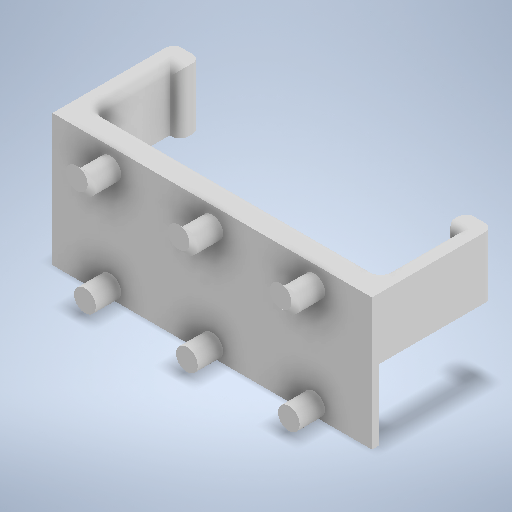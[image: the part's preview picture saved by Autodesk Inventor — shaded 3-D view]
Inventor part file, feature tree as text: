
AUTODESK INVENTOR PART (.ipt)
format: ipt  version: 2025.2 (Build 292293000, 293)  size: 474,112 bytes
history: native  units: mm
features: other x10, sketch x6, extrude x5, pattern_linear x3, fillet x3, direct_edit x3, move_body x3, chamfer x2, loft x1
ambient origin geometry x8: Origin, YZ Plane, XZ Plane, XY Plane, X Axis, Y Axis, Z Axis, Center Point
bodies: Body1 (feature_tree)
feature tree (36):
  other  "Твердое тело1"
  extrude  "Выдавливание1"  Depth=1.85mm TaperAngle=0.0deg
  extrude  "Выдавливание2"  Depth=55.2mm
  pattern_linear  "Прямоуг.массив1"  Spacing1=32.25mm  [1 undecoded]
  extrude  "Выдавливание3"  Depth=5.3mm
  extrude  "Выдавливание4"  Depth=6.2mm TaperAngle=0.0deg
  fillet  "Сопряжение1"  Radius=20.0mm
  pattern_linear  "Прямоуг.массив2"  Spacing1=24.95mm  [1 undecoded]
  fillet  "Сопряжение2"  Radius=15.0mm
  other  "РабПлоскость1"
  loft  "Лофт1"
  pattern_linear  "Прямоуг.массив3"  Count1=5  [1 undecoded]
  other  "Удаление грани1"
  extrude  "Выдавливание6"  Depth=15.0mm
  other  "Непосредственное редактирование1"
  other  "Непосредственное редактирование2"
  fillet  "Сопряжение3"  [1 undecoded]
  direct_edit  "Direct Edit3"
  direct_edit  "Direct Edit4"
  direct_edit  "Direct Edit5"
  chamfer  "Фаска1"  Distance=25.0mm
  chamfer  "Фаска2"  Distance=2.0mm
  sketch  "Эскиз1"
  sketch  "Эскиз2"
  sketch  "Эскиз3"
  sketch  "Эскиз4"
  sketch  "Эскиз7"
  other  "Ребра1"
  sketch  "Эскиз10"
  other  "Перенос1"
  other  "Перенос2"
  other  "Перенос3"
  other  "Перенос4"
  move_body  "Move5"
  move_body  "Move6"
  move_body  "Move7"
note: 4 required parameter values undecoded (feature->parameter linkage not recoverable at this tier; creation-order binding heuristic only, values carry confidence <= 0.55)
